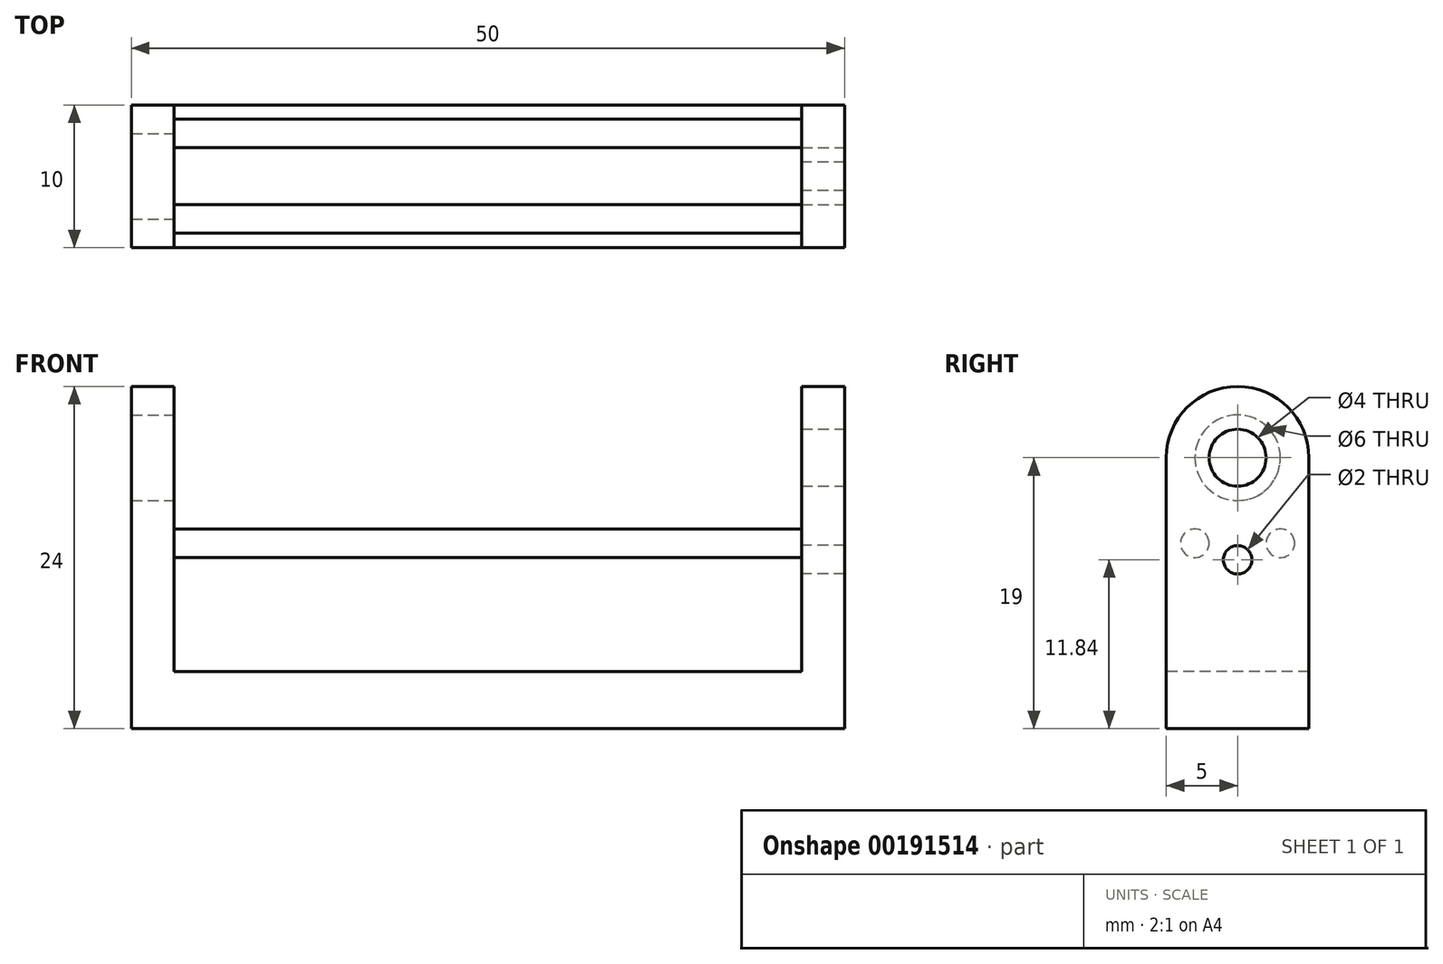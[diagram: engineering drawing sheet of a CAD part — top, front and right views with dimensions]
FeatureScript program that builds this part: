
annotation { "Feature Type Name" : "Feature", "Feature Type Description" : "" }
export const myFeature = defineFeature(function(context is Context, id is Id, definition is map)
    precondition{}
    {
        {
            var Q0;
            Q0=qCreatedBy(makeId("Top.planeOp"),FACE);
            var sketch = newSketch(context, id + "F0", { "sketchPlane" : qUnion([Q0])});
            skLineSegment(sketch, "E0.bottom", {"start": v(25, -5) * mm, "end": v(-25, -5) * mm});
            skLineSegment(sketch, "E0.top", {"start": v(25, 5) * mm, "end": v(-25, 5) * mm});
            skLineSegment(sketch, "E0.left", {"start": v(25, -5) * mm, "end": v(25, 5) * mm});
            skLineSegment(sketch, "E0.right", {"start": v(-25, -5) * mm, "end": v(-25, 5) * mm});
            skPoint(sketch, "E0.middle", {"position": v(0, 0) * mm});
            skSolve(sketch);
        }
        {
            var Q0;
            Q0=qSketchRegion(id+"F0",true);
            extrude(context, id + "F1", {"entities" : qUnion([Q0]), "depth" : 4 * mm});
        }
        {
            var Q0;
            Q0=makeQuery(id+"F1.opExtrude","CAP_FACE",FACE,{"disambiguationData":[OSD([sQuery(id+"F0.wireOp",EDGE,"E0.bottom"),sQuery(id+"F0.wireOp",EDGE,"E0.top"),sQuery(id+"F0.wireOp",EDGE,"E0.left"),sQuery(id+"F0.wireOp",EDGE,"E0.right")])],"isStart":false});
            var sketch = newSketch(context, id + "F2", { "sketchPlane" : qUnion([Q0])});
            skLineSegment(sketch, "E1.bottom", {"start": v(25, 5) * mm, "end": v(22, 5) * mm});
            skLineSegment(sketch, "E1.top", {"start": v(25, -5) * mm, "end": v(22, -5) * mm});
            skLineSegment(sketch, "E1.left", {"start": v(25, 5) * mm, "end": v(25, -5) * mm});
            skLineSegment(sketch, "E1.right", {"start": v(22, 5) * mm, "end": v(22, -5) * mm});
            skLineSegment(sketch, "E2", {"start": v(0, 0) * mm, "end": v(0, -14.5) * mm, "construction": true});
            skLineSegment(sketch, "E3.MirrorCS", {"start": v(-25, 5) * mm, "end": v(-22, 5) * mm});
            skLineSegment(sketch, "E4.MirrorCS", {"start": v(-25, -5) * mm, "end": v(-22, -5) * mm});
            skLineSegment(sketch, "E5.MirrorCS", {"start": v(-25, 5) * mm, "end": v(-25, -5) * mm});
            skLineSegment(sketch, "E6.MirrorCS", {"start": v(-22, 5) * mm, "end": v(-22, -5) * mm});
            skSolve(sketch);
        }
        {
            var Q0;
            Q0=qSketchRegion(id+"F2",true);
            extrude(context, id + "F3", {"entities" : qUnion([Q0]), "operationType" : NewBodyOperationType.ADD, "depth" : 20 * mm});
        }
        {
            var Q0;
            Q0=makeQuery(id+"F3.opExtrude","CAP_EDGE",EDGE,{"disambiguationData":[OSD([sQuery(id+"F2.wireOp",EDGE,"E4.MirrorCS")])],"isStart":false});
            var Q1;
            Q1=makeQuery(id+"F3.opExtrude","CAP_EDGE",EDGE,{"disambiguationData":[OSD([sQuery(id+"F2.wireOp",EDGE,"E3.MirrorCS")])],"isStart":false});
            var Q2;
            Q2=makeQuery(id+"F3.opExtrude","CAP_EDGE",EDGE,{"disambiguationData":[OSD([sQuery(id+"F2.wireOp",EDGE,"E1.top")])],"isStart":false});
            var Q3;
            Q3=makeQuery(id+"F3.opExtrude","CAP_EDGE",EDGE,{"disambiguationData":[OSD([sQuery(id+"F2.wireOp",EDGE,"E1.bottom")])],"isStart":false});
            fillet(context, id + "F4", {"entities" : qUnion([Q0, Q1, Q2, Q3]), "radius" : 5 * mm, "tangentPropagation" : true, "allowEdgeOverflow" : false});
        }
        {
            var Q0;
            Q0=makeQuery(id+"F3.boolean.opBoolean","MERGE",FACE,{"derivedFrom":[makeQuery(id+"F1.opExtrude","SWEPT_FACE",FACE,{"disambiguationData":[OSD([sQuery(id+"F0.wireOp",EDGE,"E0.left")])]}),makeQuery(id+"F3.opExtrude","SWEPT_FACE",FACE,{"disambiguationData":[OSD([sQuery(id+"F2.wireOp",EDGE,"E1.left")])]})]});
            var sketch = newSketch(context, id + "F5", { "sketchPlane" : qUnion([Q0])});
            skCircle(sketch, "E7", {"center": v(0, 19) * mm, "radius": 2 * mm});
            skSolve(sketch);
        }
        {
            var Q0;
            Q0=qSketchRegion(id+"F5",true);
            extrude(context, id + "F6", {"entities" : qUnion([Q0]), "operationType" : NewBodyOperationType.REMOVE, "oppositeDirection" : true, "depth" : 25 * mm});
        }
        {
            var Q0;
            Q0=makeQuery(id+"F3.opExtrude","SWEPT_FACE",FACE,{"disambiguationData":[OSD([sQuery(id+"F2.wireOp",EDGE,"E6.MirrorCS")])]});
            var sketch = newSketch(context, id + "F7", { "sketchPlane" : qUnion([Q0])});
            skCircle(sketch, "E8", {"center": v(0, 19) * mm, "radius": 3 * mm});
            skSolve(sketch);
        }
        {
            var Q0;
            Q0=qSketchRegion(id+"F7",true);
            extrude(context, id + "F8", {"entities" : qUnion([Q0]), "operationType" : NewBodyOperationType.REMOVE, "oppositeDirection" : true, "depth" : 25 * mm});
        }
        {
            var Q0;
            Q0=makeQuery(id+"F3.opExtrude","SWEPT_FACE",FACE,{"disambiguationData":[OSD([sQuery(id+"F2.wireOp",EDGE,"E6.MirrorCS")])]});
            var sketch = newSketch(context, id + "F9", { "sketchPlane" : qUnion([Q0])});
            skLineSegment(sketch, "E9", {"start": v(0, 6.78) * mm, "end": v(0, 13.12) * mm, "construction": true});
            skCircle(sketch, "E10", {"center": v(-3, 13) * mm, "radius": 1 * mm});
            skCircle(sketch, "E11", {"center": v(3, 13) * mm, "radius": 1 * mm});
            skSolve(sketch);
        }
        {
            var Q0;
            Q0=qSketchRegion(id+"F9",true);
            extrude(context, id + "F10", {"entities" : qUnion([Q0]), "operationType" : NewBodyOperationType.ADD, "depth" : 46 * mm});
        }
        {
            var Q0;
            Q0=makeQuery(id+"F3.opExtrude","SWEPT_FACE",FACE,{"disambiguationData":[OSD([sQuery(id+"F2.wireOp",EDGE,"E1.right")])]});
            var sketch = newSketch(context, id + "F11", { "sketchPlane" : qUnion([Q0])});
            skCircle(sketch, "E12", {"center": v(0, 11.84) * mm, "radius": 1 * mm});
            skLineSegment(sketch, "E13", {"start": v(3, 13) * mm, "end": v(-4, 13) * mm, "construction": true});
            skSolve(sketch);
        }
        {
            var Q0;
            Q0=qSketchRegion(id+"F11",true);
            extrude(context, id + "F12", {"entities" : qUnion([Q0]), "operationType" : NewBodyOperationType.REMOVE, "oppositeDirection" : true, "depth" : 25 * mm});
        }
    });
